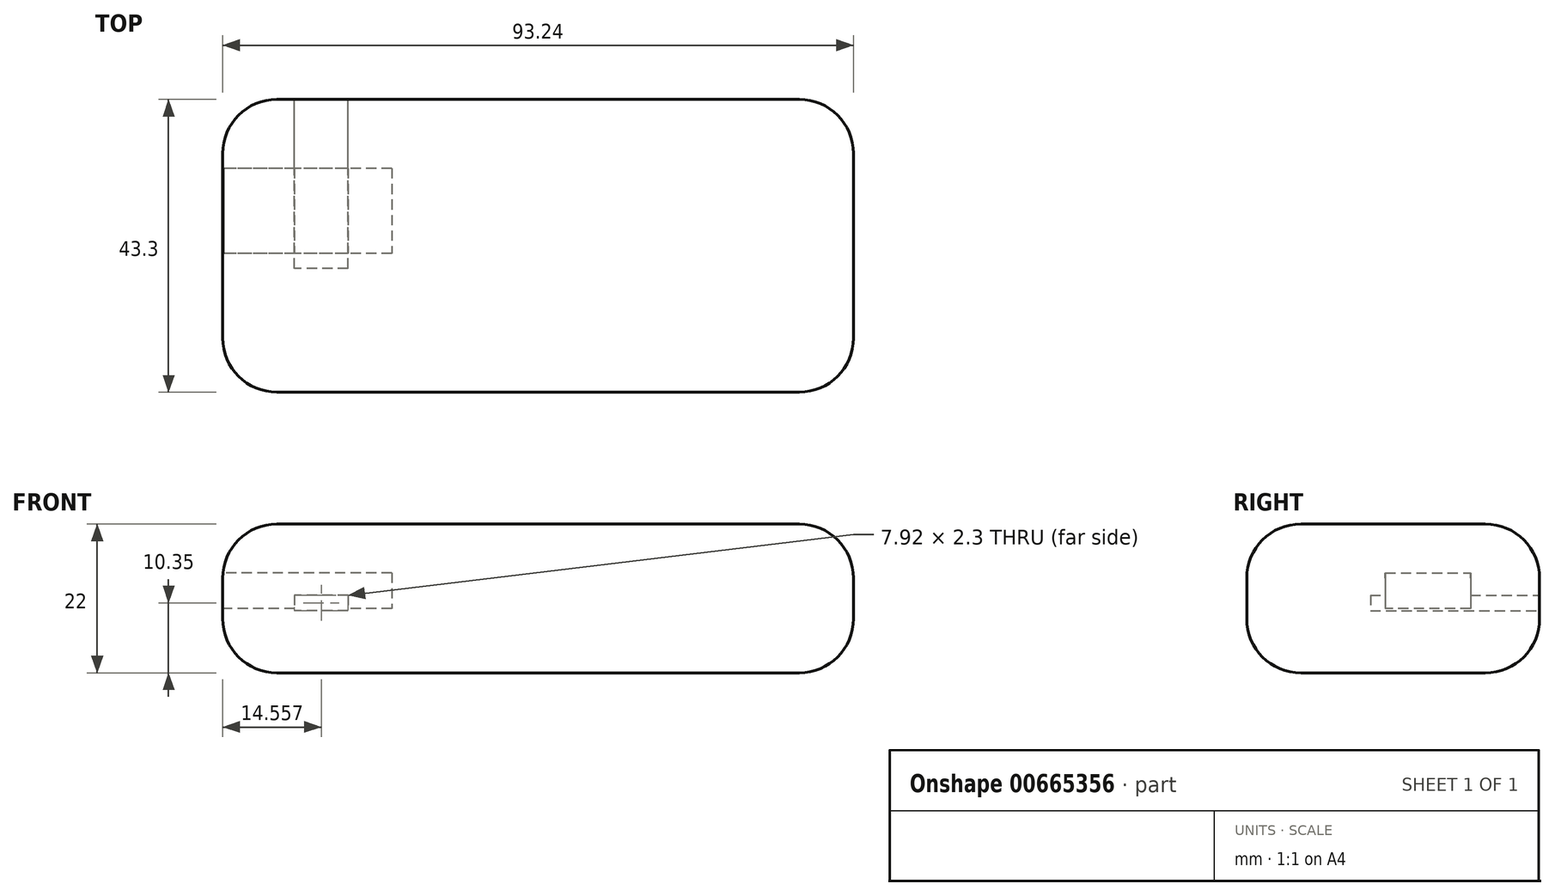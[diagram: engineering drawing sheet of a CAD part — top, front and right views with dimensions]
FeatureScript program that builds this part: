
annotation { "Feature Type Name" : "Feature", "Feature Type Description" : "" }
export const myFeature = defineFeature(function(context is Context, id is Id, definition is map)
    precondition{}
    {
        {
            var Q0;
            Q0=qCreatedBy(makeId("Top.planeOp"),FACE);
            var sketch = newSketch(context, id + "F0", { "sketchPlane" : qUnion([Q0])});
            skLineSegment(sketch, "E0.bottom", {"start": v(38.62, -21.65) * mm, "end": v(-38.62, -21.65) * mm});
            skLineSegment(sketch, "E0.top", {"start": v(38.62, 21.65) * mm, "end": v(-38.62, 21.65) * mm});
            skLineSegment(sketch, "E0.left", {"start": v(46.62, -13.65) * mm, "end": v(46.62, 13.65) * mm});
            skLineSegment(sketch, "E0.right", {"start": v(-46.62, -13.65) * mm, "end": v(-46.62, 13.65) * mm});
            skPoint(sketch, "E0.middle", {"position": v(0, 0) * mm});
            skPoint(sketch, "E1.visualSharp", {"position": v(46.62, 21.65) * mm});
            skArc(sketch, "E1.filletArc", {"start": v(46.62, 13.65) * mm, "mid": v(44.28, 19.3) * mm, "end": v(38.62, 21.65) * mm});
            skPoint(sketch, "E2.visualSharp", {"position": v(-46.62, 21.65) * mm});
            skArc(sketch, "E2.filletArc", {"start": v(-38.62, 21.65) * mm, "mid": v(-44.28, 19.3) * mm, "end": v(-46.62, 13.65) * mm});
            skPoint(sketch, "E3.visualSharp", {"position": v(-46.62, -21.65) * mm});
            skArc(sketch, "E3.filletArc", {"start": v(-46.62, -13.65) * mm, "mid": v(-44.28, -19.3) * mm, "end": v(-38.62, -21.65) * mm});
            skPoint(sketch, "E4.visualSharp", {"position": v(46.62, -21.65) * mm});
            skArc(sketch, "E4.filletArc", {"start": v(38.62, -21.65) * mm, "mid": v(44.28, -19.3) * mm, "end": v(46.62, -13.65) * mm});
            skSolve(sketch);
        }
        {
            var Q0;
            Q0 = qSketchRegion(id + "F0", true);
            extrude(context, id + "F1", {"entities" : qUnion([Q0]), "endBound" : BoundingType.SYMMETRIC, "depth" : 22 * mm, "offsetDistance" : 25 * mm});
        }
        {
            var Q0;
            Q0=makeQuery(id+"F1.opExtrude","CAP_FACE",FACE,{"disambiguationData":[OSD([sQuery(id+"F0.wireOp",EDGE,"E0.bottom"),sQuery(id+"F0.wireOp",EDGE,"E0.top"),sQuery(id+"F0.wireOp",EDGE,"E0.left"),sQuery(id+"F0.wireOp",EDGE,"E0.right"),sQuery(id+"F0.wireOp",EDGE,"E1.filletArc"),sQuery(id+"F0.wireOp",EDGE,"E2.filletArc"),sQuery(id+"F0.wireOp",EDGE,"E3.filletArc"),sQuery(id+"F0.wireOp",EDGE,"E4.filletArc")])],"isStart":false});
            var Q1;
            Q1=makeQuery(id+"F1.opExtrude","CAP_FACE",FACE,{"disambiguationData":[OSD([sQuery(id+"F0.wireOp",EDGE,"E0.bottom"),sQuery(id+"F0.wireOp",EDGE,"E0.top"),sQuery(id+"F0.wireOp",EDGE,"E0.left"),sQuery(id+"F0.wireOp",EDGE,"E0.right"),sQuery(id+"F0.wireOp",EDGE,"E1.filletArc"),sQuery(id+"F0.wireOp",EDGE,"E2.filletArc"),sQuery(id+"F0.wireOp",EDGE,"E3.filletArc"),sQuery(id+"F0.wireOp",EDGE,"E4.filletArc")])],"isStart":true});
            fillet(context, id + "F2", {"entities" : qUnion([Q0, Q1]), "radius" : 8 * mm, "tangentPropagation" : true, "allowEdgeOverflow" : false});
        }
        {
            var Q0;
            Q0=makeQuery(id+"F1.opExtrude","SWEPT_FACE",FACE,{"disambiguationData":[OSD([sQuery(id+"F0.wireOp",EDGE,"E0.right")])]});
            var sketch = newSketch(context, id + "F3", { "sketchPlane" : qUnion([Q0])});
            skLineSegment(sketch, "E5.bottom", {"start": v(-11.45, 3.8) * mm, "end": v(1.15, 3.8) * mm});
            skLineSegment(sketch, "E5.top", {"start": v(-11.45, -1.5) * mm, "end": v(1.15, -1.5) * mm});
            skLineSegment(sketch, "E5.left", {"start": v(-11.45, 3.8) * mm, "end": v(-11.45, -1.5) * mm});
            skLineSegment(sketch, "E5.right", {"start": v(1.15, 3.8) * mm, "end": v(1.15, -1.5) * mm});
            skLineSegment(sketch, "E6.0.0", {"start": v(-21.65, 3) * mm, "end": v(-21.65, -3) * mm, "construction": true});
            skLineSegment(sketch, "E6.0.2", {"start": v(-21.65, -3) * mm, "end": v(-21.65, 3) * mm, "construction": true});
            skLineSegment(sketch, "E7.0.0", {"start": v(-13.65, 11) * mm, "end": v(-13.65, 3) * mm, "construction": true});
            skLineSegment(sketch, "E7.0.1", {"start": v(-13.65, 3) * mm, "end": v(13.65, 3) * mm, "construction": true});
            skLineSegment(sketch, "E7.0.2", {"start": v(13.65, 3) * mm, "end": v(13.65, 11) * mm, "construction": true});
            skLineSegment(sketch, "E7.0.3", {"start": v(-13.65, 11) * mm, "end": v(13.65, 11) * mm, "construction": true});
            skSolve(sketch);
        }
        {
            var Q0;
            Q0 = qSketchRegion(id + "F3", true);
            extrude(context, id + "F4", {"entities" : qUnion([Q0]), "operationType" : NewBodyOperationType.REMOVE, "oppositeDirection" : true, "depth" : 25 * mm, "offsetDistance" : 25 * mm});
        }
        {
            var Q0;
            Q0=makeQuery(id+"F1.opExtrude","SWEPT_FACE",FACE,{"disambiguationData":[OSD([sQuery(id+"F0.wireOp",EDGE,"E0.top")])]});
            var sketch = newSketch(context, id + "F5", { "sketchPlane" : qUnion([Q0])});
            skPoint(sketch, "E8.oppositeSnap0", {"position": v(38.62, 0) * mm});
            skLineSegment(sketch, "E8.bottom", {"start": v(28.1, 0.5) * mm, "end": v(36.02, 0.5) * mm});
            skLineSegment(sketch, "E8.top", {"start": v(28.1, -1.8) * mm, "end": v(36.02, -1.8) * mm});
            skLineSegment(sketch, "E8.left", {"start": v(28.1, 0.5) * mm, "end": v(28.1, -1.8) * mm});
            skLineSegment(sketch, "E8.right", {"start": v(36.02, 0.5) * mm, "end": v(36.02, -1.8) * mm});
            skLineSegment(sketch, "E9.0.0", {"start": v(38.63, -11) * mm, "end": v(38.63, -3) * mm, "construction": true});
            skLineSegment(sketch, "E9.0.1", {"start": v(38.62, -3) * mm, "end": v(-38.62, -3) * mm, "construction": true});
            skLineSegment(sketch, "E9.0.2", {"start": v(-38.62, -3) * mm, "end": v(-38.62, -11) * mm, "construction": true});
            skLineSegment(sketch, "E9.0.3", {"start": v(38.63, -11) * mm, "end": v(-38.62, -11) * mm, "construction": true});
            skLineSegment(sketch, "E10.0.0", {"start": v(38.62, 3) * mm, "end": v(38.62, -3) * mm, "construction": true});
            skLineSegment(sketch, "E10.0.1", {"start": v(38.62, -3) * mm, "end": v(46.62, -3) * mm, "construction": true});
            skLineSegment(sketch, "E10.0.2", {"start": v(46.62, -3) * mm, "end": v(46.62, 3) * mm, "construction": true});
            skLineSegment(sketch, "E10.0.3", {"start": v(46.62, 3) * mm, "end": v(38.62, 3) * mm, "construction": true});
            skSolve(sketch);
        }
        {
            var Q0;
            Q0 = qSketchRegion(id + "F5", true);
            extrude(context, id + "F6", {"entities" : qUnion([Q0]), "operationType" : NewBodyOperationType.REMOVE, "oppositeDirection" : true, "depth" : 25 * mm, "offsetDistance" : 25 * mm});
        }
    });
